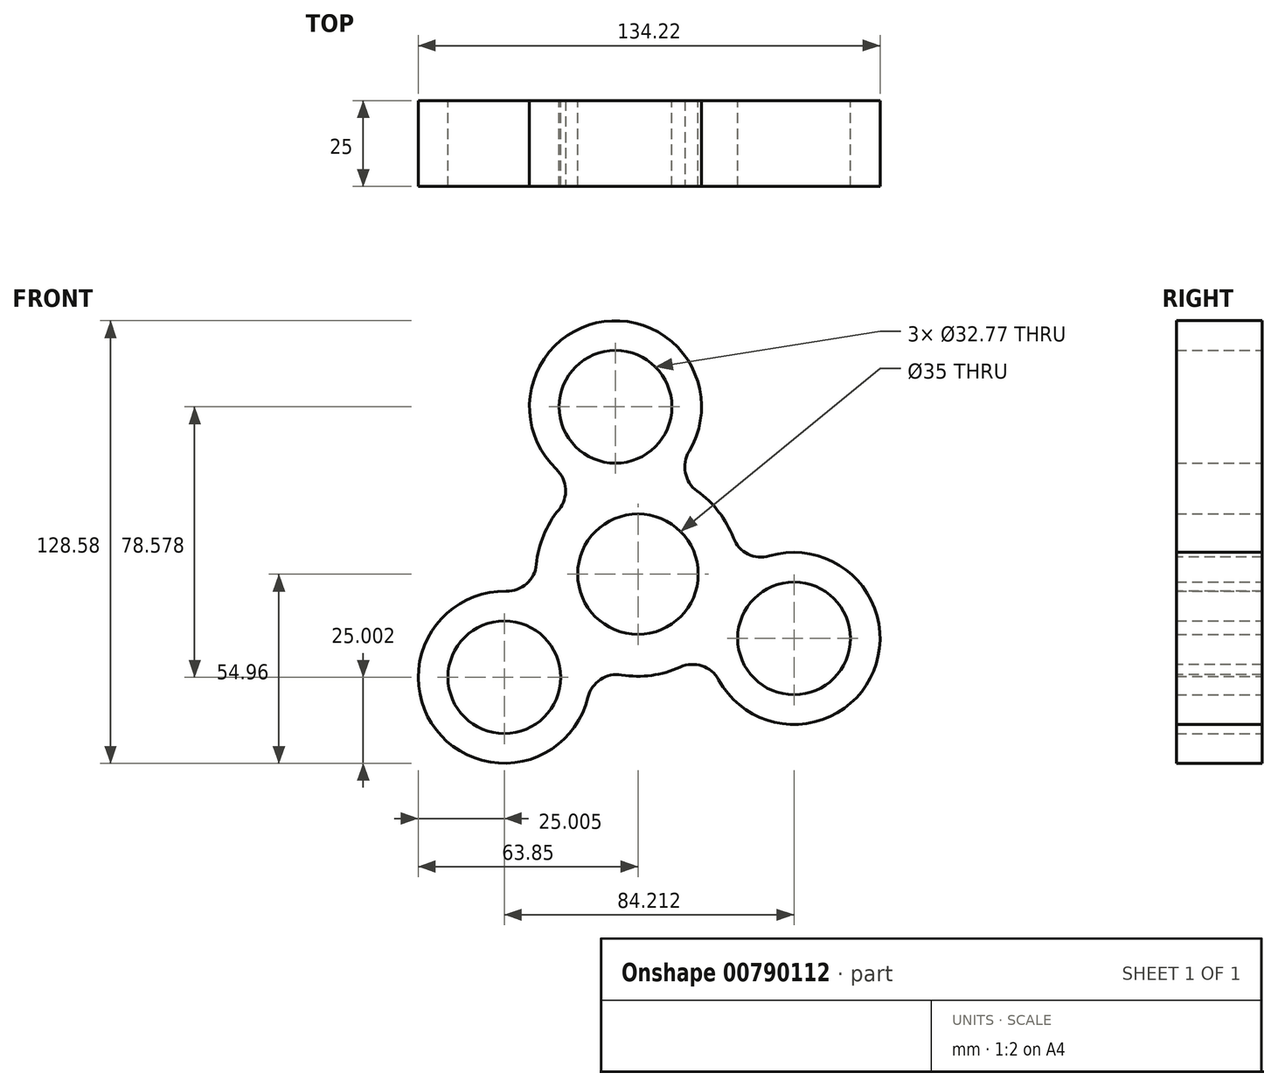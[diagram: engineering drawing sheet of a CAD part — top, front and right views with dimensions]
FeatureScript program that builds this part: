
annotation { "Feature Type Name" : "Feature", "Feature Type Description" : "" }
export const myFeature = defineFeature(function(context is Context, id is Id, definition is map)
    precondition{}
    {
        {
            var Q0;
            Q0=qCreatedBy(makeId("Front.planeOp"),FACE);
            var sketch = newSketch(context, id + "F0", { "sketchPlane" : qUnion([Q0])});
            skCircle(sketch, "E0", {"center": v(0, 0) * mm, "radius": 29.65 * mm});
            skCircle(sketch, "E1", {"center": v(0, 0) * mm, "radius": 17.5 * mm});
            skCircle(sketch, "E2", {"center": v(-38.85, -29.96) * mm, "radius": 25 * mm});
            skCircle(sketch, "E3", {"center": v(-38.85, -29.96) * mm, "radius": 16.38 * mm});
            skCircle(sketch, "E4.1.0", {"center": v(45.37, -18.66) * mm, "radius": 16.38 * mm});
            skCircle(sketch, "E4.1.1", {"center": v(45.37, -18.66) * mm, "radius": 25 * mm});
            skCircle(sketch, "E4.2.0", {"center": v(-6.52, 48.62) * mm, "radius": 16.38 * mm});
            skCircle(sketch, "E4.2.1", {"center": v(-6.52, 48.62) * mm, "radius": 25 * mm});
            skSolve(sketch);
        }
        {
            var Q0;
            Q0=makeQuery(id+"F0.imprint","IMPRINT",FACE,{"disambiguationData":[TD([[makeQuery(id+"F0.imprint","IMPRINT",EDGE,{"derivedFrom":sQuery(id+"F0.wireOp",EDGE,"E4.2.0")}),-1.0]])]});
            var Q1;
            Q1=makeQuery(id+"F0.imprint","IMPRINT",FACE,{"disambiguationData":[TD([[makeQuery(id+"F0.imprint","IMPRINT",EDGE,{"derivedFrom":sQuery(id+"F0.wireOp",EDGE,"E1")}),-1.0]])]});
            var Q2;
            {var subQ0=sQuery(id+"F0.wireOp",EDGE,"E4.2.1");var subQ1=sQuery(id+"F0.wireOp",EDGE,"E0");var subQ2=makeQuery(id+"F0.imprint","INTERSECT",VERTEX,{"disambiguationData":[OD(0.0)],"derivedFrom":[subQ1,subQ0]});Q2=makeQuery(id+"F0.imprint","IMPRINT",FACE,{"disambiguationData":[TD([[makeQuery(id+"F0.imprint","IMPRINT",EDGE,{"disambiguationData":[TD([[subQ2,-1.0]])],"derivedFrom":subQ1}),1.0]])]});}
            var Q3;
            Q3=makeQuery(id+"F0.imprint","IMPRINT",FACE,{"disambiguationData":[TD([[makeQuery(id+"F0.imprint","IMPRINT",EDGE,{"derivedFrom":sQuery(id+"F0.wireOp",EDGE,"E3")}),-1.0]])]});
            var Q4;
            Q4=makeQuery(id+"F0.imprint","IMPRINT",FACE,{"disambiguationData":[TD([[makeQuery(id+"F0.imprint","IMPRINT",EDGE,{"derivedFrom":sQuery(id+"F0.wireOp",EDGE,"E4.1.0")}),-1.0]])]});
            var Q5;
            {var subQ0=sQuery(id+"F0.wireOp",EDGE,"E4.1.1");var subQ1=sQuery(id+"F0.wireOp",EDGE,"E0");var subQ2=makeQuery(id+"F0.imprint","INTERSECT",VERTEX,{"disambiguationData":[OD(0.0)],"derivedFrom":[subQ1,subQ0]});Q5=makeQuery(id+"F0.imprint","IMPRINT",FACE,{"disambiguationData":[TD([[makeQuery(id+"F0.imprint","IMPRINT",EDGE,{"disambiguationData":[TD([[subQ2,1.0]])],"derivedFrom":subQ1}),1.0]])]});}
            var Q6;
            {var subQ0=sQuery(id+"F0.wireOp",EDGE,"E2");var subQ1=sQuery(id+"F0.wireOp",EDGE,"E0");var subQ2=makeQuery(id+"F0.imprint","INTERSECT",VERTEX,{"disambiguationData":[OD(0.0)],"derivedFrom":[subQ1,subQ0]});Q6=makeQuery(id+"F0.imprint","IMPRINT",FACE,{"disambiguationData":[TD([[makeQuery(id+"F0.imprint","IMPRINT",EDGE,{"disambiguationData":[TD([[subQ2,-1.0]])],"derivedFrom":subQ1}),1.0]])]});}
            extrude(context, id + "F1", {"entities" : qUnion([Q0, Q1, Q2, Q3, Q4, Q5, Q6]), "endBound" : BoundingType.SYMMETRIC, "depth" : 25 * mm, "offsetDistance" : 25 * mm});
        }
        {
            var Q0;
            {var subQ0=sQuery(id+"F0.wireOp",EDGE,"E2");var subQ1=sQuery(id+"F0.wireOp",EDGE,"E0");Q0=makeQuery(id+"F1.opExtrude","SWEPT_EDGE",EDGE,{"disambiguationData":[OSD([subQ1,subQ0]),TDD([makeQuery(id+"F0.imprint","INTERSECT",VERTEX,{"disambiguationData":[OD(0.0)],"derivedFrom":[subQ1,subQ0]})])]});}
            var Q1;
            {var subQ0=sQuery(id+"F0.wireOp",EDGE,"E4.2.1");var subQ1=sQuery(id+"F0.wireOp",EDGE,"E0");Q1=makeQuery(id+"F1.opExtrude","SWEPT_EDGE",EDGE,{"disambiguationData":[OSD([subQ1,subQ0]),TDD([makeQuery(id+"F0.imprint","INTERSECT",VERTEX,{"disambiguationData":[OD(1.0)],"derivedFrom":[subQ1,subQ0]})])]});}
            var Q2;
            {var subQ0=sQuery(id+"F0.wireOp",EDGE,"E2");var subQ1=sQuery(id+"F0.wireOp",EDGE,"E0");Q2=makeQuery(id+"F1.opExtrude","SWEPT_EDGE",EDGE,{"disambiguationData":[OSD([subQ1,subQ0]),TDD([makeQuery(id+"F0.imprint","INTERSECT",VERTEX,{"disambiguationData":[OD(1.0)],"derivedFrom":[subQ1,subQ0]})])]});}
            var Q3;
            {var subQ0=sQuery(id+"F0.wireOp",EDGE,"E4.1.1");var subQ1=sQuery(id+"F0.wireOp",EDGE,"E0");Q3=makeQuery(id+"F1.opExtrude","SWEPT_EDGE",EDGE,{"disambiguationData":[OSD([subQ1,subQ0]),TDD([makeQuery(id+"F0.imprint","INTERSECT",VERTEX,{"disambiguationData":[OD(1.0)],"derivedFrom":[subQ1,subQ0]})])]});}
            var Q4;
            {var subQ0=sQuery(id+"F0.wireOp",EDGE,"E4.2.1");var subQ1=sQuery(id+"F0.wireOp",EDGE,"E0");Q4=makeQuery(id+"F1.opExtrude","SWEPT_EDGE",EDGE,{"disambiguationData":[OSD([subQ1,subQ0]),TDD([makeQuery(id+"F0.imprint","INTERSECT",VERTEX,{"disambiguationData":[OD(0.0)],"derivedFrom":[subQ1,subQ0]})])]});}
            var Q5;
            {var subQ0=sQuery(id+"F0.wireOp",EDGE,"E4.1.1");var subQ1=sQuery(id+"F0.wireOp",EDGE,"E0");Q5=makeQuery(id+"F1.opExtrude","SWEPT_EDGE",EDGE,{"disambiguationData":[OSD([subQ1,subQ0]),TDD([makeQuery(id+"F0.imprint","INTERSECT",VERTEX,{"disambiguationData":[OD(0.0)],"derivedFrom":[subQ1,subQ0]})])]});}
            fillet(context, id + "F2", {"entities" : qUnion([Q0, Q1, Q2, Q3, Q4, Q5]), "radius" : 8.65 * mm, "tangentPropagation" : true, "allowEdgeOverflow" : false});
        }
    });
